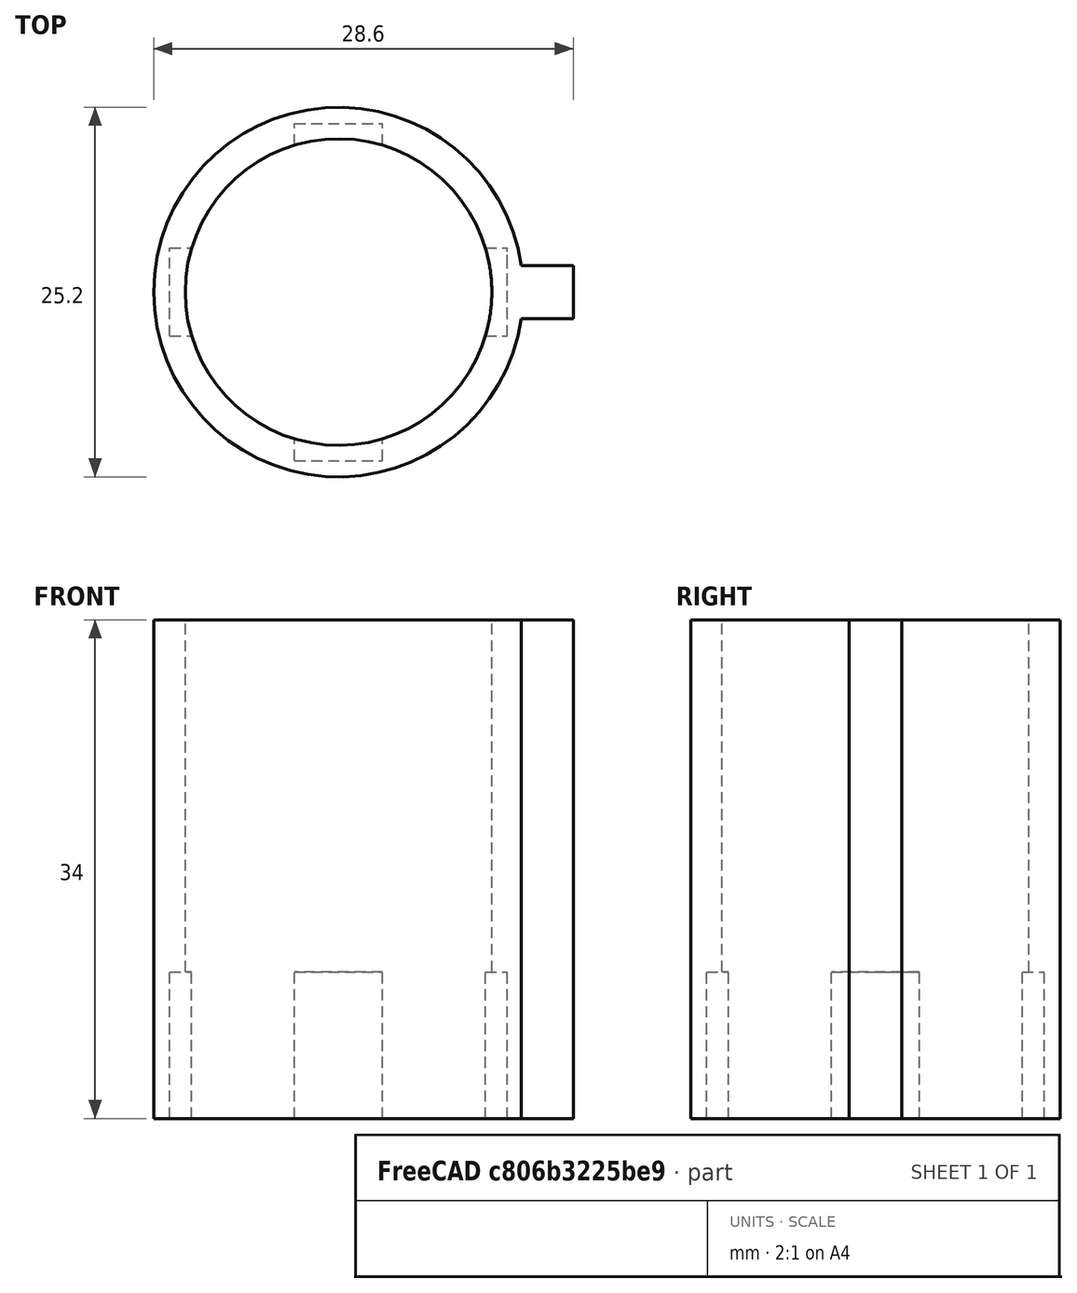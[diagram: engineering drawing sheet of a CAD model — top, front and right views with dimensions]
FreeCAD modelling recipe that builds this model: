
FCSTD DOCUMENT  (FreeCAD 0.15R4671 (Git))
Label: 200-core
License: All rights reserved
LicenseURL: http://en.wikipedia.org/wiki/All_rights_reserved
objects: Part::Box×3, Part::Cut×3, Part::Cylinder×2, Part::MultiFuse×1
note: 9 computed .brp shape members not serialized (recipe doc carries the construction recipe); baked Part::Feature solids carry a one-line shape summary decoded from their .brp

FEATURE [Part::Cylinder] Cylinder  label="Outside"
  Angle = 360
  Height = 34
  Radius = 12.6
FEATURE [Part::Box] Box  label="Tab"
  Height = 34
  Length = 10
  Placement = pos=(6,-1.8,0) rot=(0,0,1;0rad)
  Width = 3.6
FEATURE [Part::Cylinder] Cylinder001  label="Cylinder"
  Angle = 360
  Height = 100
  Radius = 10.45
FEATURE [Part::MultiFuse] Fusion
  Shapes = -> [Box,Cylinder]
FEATURE [Part::Cut] Cut
  Base = -> Fusion
  Tool = -> Cylinder001
FEATURE [Part::Box] Box001  label="Cube"
  Height = 10
  Length = 23
  Placement = pos=(-11.5,-3,0) rot=(0,0,1;0rad)
  Width = 6
FEATURE [Part::Box] Box002  label="Cube001"
  Height = 10
  Length = 6
  Placement = pos=(-3,-11.5,0) rot=(0,0,1;0rad)
  Width = 23
FEATURE [Part::Cut] Cut001
  Base = -> Cut
  Tool = -> Box002
FEATURE [Part::Cut] Cut002  label="Final"
  Base = -> Cut001
  Tool = -> Box001
